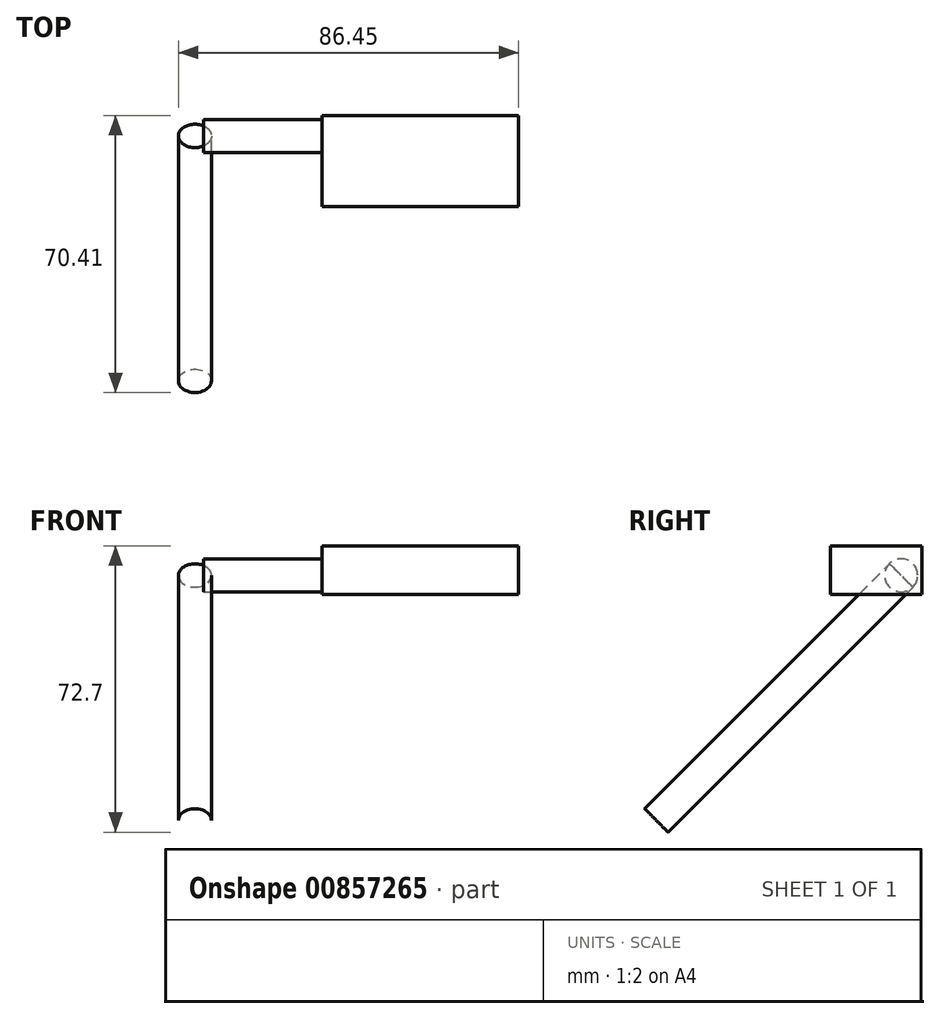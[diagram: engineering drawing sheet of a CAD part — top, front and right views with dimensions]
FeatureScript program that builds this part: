
annotation { "Feature Type Name" : "Feature", "Feature Type Description" : "" }
export const myFeature = defineFeature(function(context is Context, id is Id, definition is map)
    precondition{}
    {
        {
            var Q0;
            Q0=qCreatedBy(makeId("Top.planeOp"),FACE);
            var sketch = newSketch(context, id + "F0", { "sketchPlane" : qUnion([Q0])});
            skLineSegment(sketch, "E0.bottom", {"start": v(25, 11.58) * mm, "end": v(-25, 11.58) * mm});
            skLineSegment(sketch, "E0.top", {"start": v(25, -11.58) * mm, "end": v(-25, -11.58) * mm});
            skLineSegment(sketch, "E0.left", {"start": v(25, 11.58) * mm, "end": v(25, -11.58) * mm});
            skLineSegment(sketch, "E0.right", {"start": v(-25, 11.58) * mm, "end": v(-25, -11.58) * mm});
            skPoint(sketch, "E0.middle", {"position": v(0, 0) * mm});
            skSolve(sketch);
        }
        {
            var Q0;
            Q0=makeQuery(id+"F0.imprint","IMPRINT",FACE,{"disambiguationData":[TD([[makeQuery(id+"F0.imprint","IMPRINT",EDGE,{"derivedFrom":sQuery(id+"F0.wireOp",EDGE,"E0.bottom")}),1.0]])]});
            extrude(context, id + "F1", {"entities" : qUnion([Q0]), "depth" : 12.3 * mm, "offsetDistance" : 25 * mm});
        }
        {
            var Q0;
            Q0=makeQuery(id+"F1.opExtrude","SWEPT_FACE",FACE,{"disambiguationData":[OSD([sQuery(id+"F0.wireOp",EDGE,"E0.right")])]});
            var sketch = newSketch(context, id + "F2", { "sketchPlane" : qUnion([Q0])});
            skCircle(sketch, "E1", {"center": v(-6.33, 4.83) * mm, "radius": 4.2 * mm});
            skSolve(sketch);
        }
        {
            var Q0;
            Q0=makeQuery(id+"F2.imprint","IMPRINT",FACE,{"disambiguationData":[TD([[makeQuery(id+"F2.imprint","IMPRINT",EDGE,{"derivedFrom":sQuery(id+"F2.wireOp",EDGE,"E1")}),1.0]])]});
            extrude(context, id + "F3", {"entities" : qUnion([Q0]), "operationType" : NewBodyOperationType.ADD, "depth" : 30 * mm, "offsetDistance" : 25 * mm});
        }
        {
            var Q0;
            Q0=sQuery(id+"F2.wireOp",VERTEX,"E1.center");
            var Q1;
            Q1=qCreatedBy(makeId("Top.planeOp"),FACE);
            cPlane(context, id + "F4", {"entities" : qUnion([Q0, Q1]), "cplaneType" : CPlaneType.PLANE_POINT, "offset" : 25 * mm, "width" : 150 * mm, "height" : 150 * mm});
        }
        {
            var Q0;
            Q0=qCreatedBy(id+"F4.planeOp",FACE);
            var sketch = newSketch(context, id + "F5", { "sketchPlane" : qUnion([Q0])});
            skCircle(sketch, "E2", {"center": v(-57.25, 6.28) * mm, "radius": 4.2 * mm});
            skSolve(sketch);
        }
        {
            var Q0;
            Q0=makeQuery(id+"F5.imprint","IMPRINT",FACE,{"disambiguationData":[TD([[makeQuery(id+"F5.imprint","IMPRINT",EDGE,{"derivedFrom":sQuery(id+"F5.wireOp",EDGE,"E2")}),1.0]])]});
            extrude(context, id + "F6", {"entities" : qUnion([Q0]), "depth" : 88 * mm, "offsetDistance" : 25 * mm});
        }
        {
            var Q0;
            Q0=makeQuery(id+"F6.opExtrude","SWEPT_BODY",BODY,{"disambiguationData":[OSD([sQuery(id+"F5.wireOp",EDGE,"E2")])]});
            var Q1;
            Q1=makeQuery(id+"F3.opExtrude","SWEPT_FACE",FACE,{"disambiguationData":[OSD([sQuery(id+"F2.wireOp",EDGE,"E1")])]});
            transform(context, id + "F7", {"entities" : qUnion([Q0]), "transformType" : TransformType.ROTATION, "transformAxis" : qUnion([Q1]), "angle" : 135 * degree, "makeCopy" : false});
        }
    });
